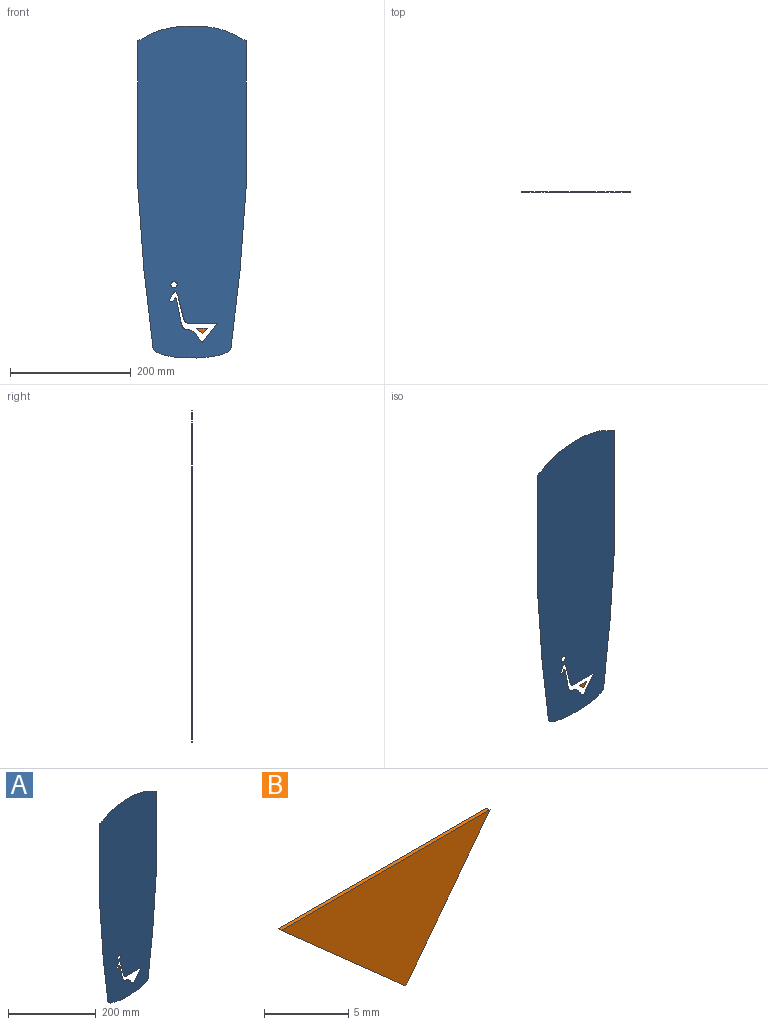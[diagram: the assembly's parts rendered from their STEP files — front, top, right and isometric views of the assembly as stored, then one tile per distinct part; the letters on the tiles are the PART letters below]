
ASSEMBLY  parts=2 mates=1
PART A: 20 faces, bbox 180.3x0.3x549.8 mm
  f0: plane 549.84x180.31mm, normal (0,-1,0), area 88823.1mm2, adj f1,f2,f3,f4,f5,f6,f7,f8
  f1: cylinder r=73.04mm len=16.8mm, axis (0,1,0), area 4.8mm2, adj f0,f2,f12,f13
  f2: extruded ~146.72x16.56mm, area 38.7mm2, adj f0,f1,f3,f13
  f3: cylinder r=73.04mm len=16.8mm, axis (0,1,0), area 4.8mm2, adj f0,f2,f4,f13
  f4: plane 234.25x0.25mm, normal (-1,0,0), area 59.5mm2, adj f0,f3,f5,f13
  f5: plane 145.81x10.65mm, normal (-1,0,-0.07), area 37.1mm2, adj f0,f4,f6,f13
  f6: plane 129.05x15.11mm, normal (-0.99,0,-0.12), area 33mm2, adj f0,f5,f7,f13
  f7: plane 1.92x1.04mm, normal (-0.88,0,-0.48), area 0.6mm2, adj f0,f6,f8,f13
  f8: extruded ~126.73x14.07mm, area 33.7mm2, adj f0,f7,f9,f13
  f9: plane 1.92x1.04mm, normal (0.88,0,-0.48), area 0.6mm2, adj f0,f8,f10,f13
  f10: plane 129.05x15.11mm, normal (0.99,0,-0.12), area 33mm2, adj f0,f9,f11,f13
  f11: plane 145.81x10.65mm, normal (1,0,-0.07), area 37.1mm2, adj f0,f10,f12,f13
  f12: plane 234.25x0.25mm, normal (1,0,0), area 59.5mm2, adj f0,f1,f11,f13
  f13: plane 549.84x180.31mm, normal (0,1,0), area 88823.1mm2, adj f1,f2,f3,f4,f5,f6,f7,f8
  f14: extruded ~52.25x29.69mm, area 19.3mm2, adj f0,f13,f15,f18
  f15: plane 5.94x1.48mm, normal (0.24,0,0.97), area 1.6mm2, adj f0,f13,f14,f16
  f16: extruded ~74.31x48.24mm, area 25.6mm2, adj f0,f13,f15,f17
  f17: plane 32.65x25.23mm, normal (-0.79,0,0.61), area 10.5mm2, adj f0,f13,f16,f18
  f18: plane 49.72x0.25mm, normal (0,0,-1), area 12.6mm2, adj f0,f13,f14,f17
  f19: cylinder r=5.16mm len=10.31mm, axis (0,1,0), area 8.2mm2, adj f0,f13
PART B: 5 faces, bbox 17.5x0.3x9.3 mm
  f0: plane 17.54x9.28mm, normal (0,1,0), area 81.3mm2, adj f1,f2,f3
  f1: plane 9.28x7.05mm, normal (0.8,0,-0.61), area 3mm2, adj f0,f2,f3,f4
  f2: plane 17.54x0.25mm, normal (0,0,1), area 4.5mm2, adj f0,f1,f3,f4
  f3: plane 10.49x9.28mm, normal (-0.66,0,-0.75), area 3.6mm2, adj f0,f1,f2,f4
  f4: plane 17.54x9.28mm, normal (0,-1,0), area 81.3mm2, adj f1,f2,f3
PLACE A t=(-202.59,0.26,-28.34)mm
PLACE B t=(-202.19,0.26,-29.26)mm
MATE fastened B.f4 <-> A.f0  axis (0,-1,0) through (-177.71,0.01,-59.81)mm
